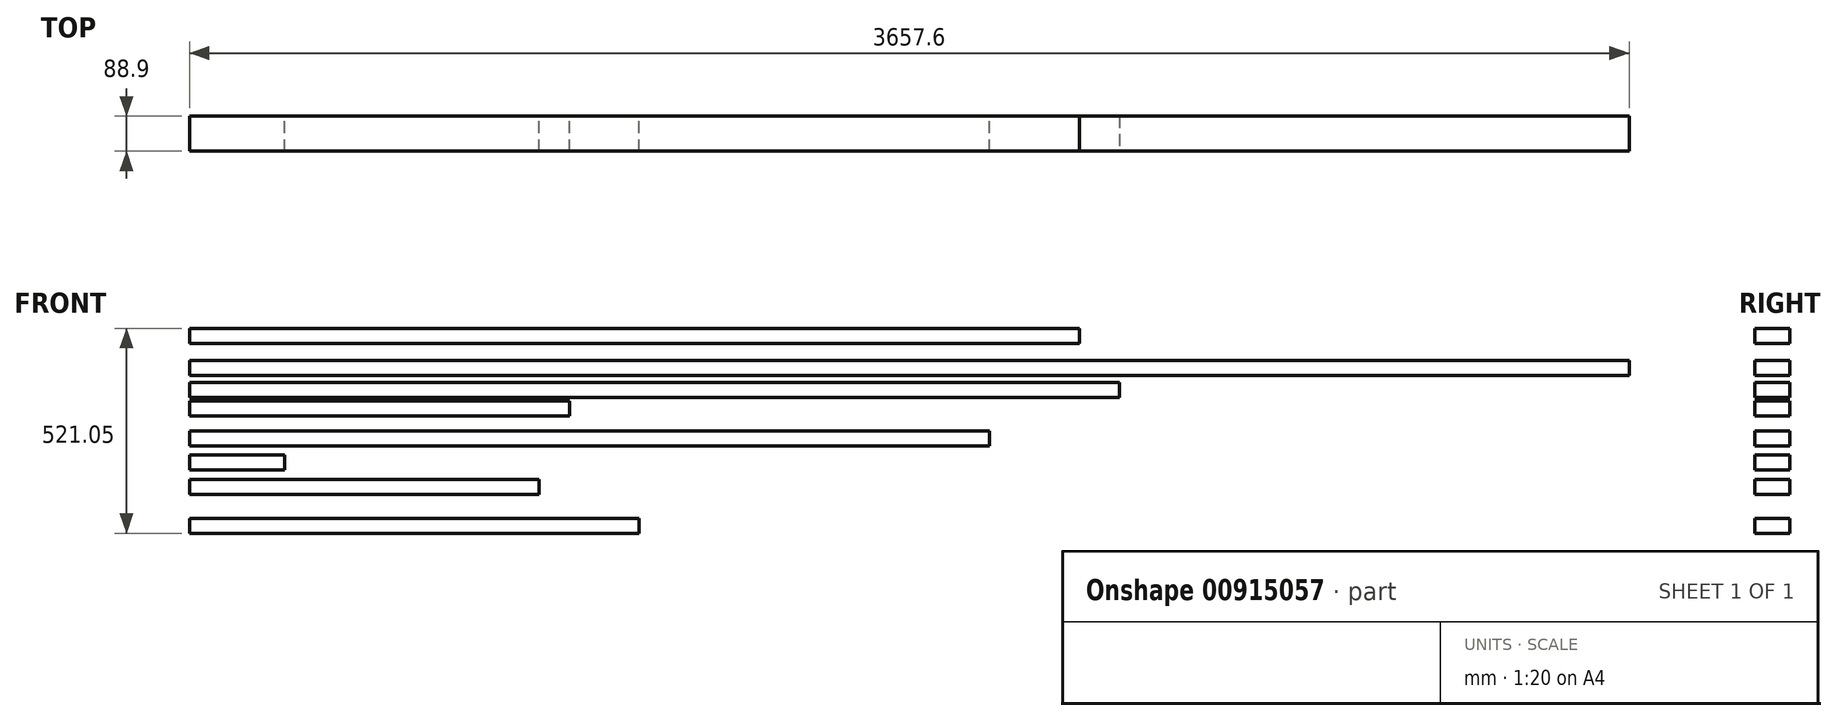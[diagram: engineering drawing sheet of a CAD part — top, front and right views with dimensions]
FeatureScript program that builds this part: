
annotation { "Feature Type Name" : "Feature", "Feature Type Description" : "" }
export const myFeature = defineFeature(function(context is Context, id is Id, definition is map)
    precondition{}
    {
        {
            var Q0;
            Q0=qCreatedBy(makeId("Right.planeOp"),FACE);
            var sketch = newSketch(context, id + "F0", { "sketchPlane" : qUnion([Q0])});
            skLineSegment(sketch, "E0.bottom", {"start": v(-44.45, -19.05) * mm, "end": v(44.45, -19.05) * mm});
            skLineSegment(sketch, "E0.top", {"start": v(-44.45, 19.05) * mm, "end": v(44.45, 19.05) * mm});
            skLineSegment(sketch, "E0.left", {"start": v(-44.45, -19.05) * mm, "end": v(-44.45, 19.05) * mm});
            skLineSegment(sketch, "E0.right", {"start": v(44.45, -19.05) * mm, "end": v(44.45, 19.05) * mm});
            skPoint(sketch, "E0.middle", {"position": v(0, 0) * mm});
            skSolve(sketch);
        }
        {
            var Q0;
            Q0=makeQuery(id+"F0.imprint","IMPRINT",FACE,{"disambiguationData":[TD([[makeQuery(id+"F0.imprint","IMPRINT",EDGE,{"derivedFrom":sQuery(id+"F0.wireOp",EDGE,"E0.bottom")}),1.0]])]});
            extrude(context, id + "F1", {"entities" : qUnion([Q0]), "depth" : 3657.6 * mm, "offsetDistance" : 25.4 * mm});
        }
        {
            var Q0;
            Q0=makeQuery(id+"F1.opExtrude","SWEPT_BODY",BODY,{"disambiguationData":[OSD([sQuery(id+"F0.wireOp",EDGE,"E0.bottom"),sQuery(id+"F0.wireOp",EDGE,"E0.top"),sQuery(id+"F0.wireOp",EDGE,"E0.left"),sQuery(id+"F0.wireOp",EDGE,"E0.right")])]});
            transform(context, id + "F2", {"entities" : qUnion([Q0]), "transformType" : TransformType.TRANSLATION_3D, "dx" : 0 * mm, "dy" : 0 * mm, "dz" : 52.83 * mm, "makeCopy" : true});
        }
        {
            var Q0;
            Q0=makeQuery(id+"F2.opPattern","COPY",BODY,{"derivedFrom":makeQuery(id+"F1.opExtrude","SWEPT_BODY",BODY,{"disambiguationData":[OSD([sQuery(id+"F0.wireOp",EDGE,"E0.bottom"),sQuery(id+"F0.wireOp",EDGE,"E0.top"),sQuery(id+"F0.wireOp",EDGE,"E0.left"),sQuery(id+"F0.wireOp",EDGE,"E0.right")])]}),"instanceName":"1"});
            deleteBodies(context, id + "F3", {"entities" : qUnion([Q0])});
        }
        {
            var Q0;
            Q0=qCreatedBy(makeId("Right.planeOp"),FACE);
            var sketch = newSketch(context, id + "F4", { "sketchPlane" : qUnion([Q0])});
            skLineSegment(sketch, "E1.bottom", {"start": v(44.45, -75.15) * mm, "end": v(-44.45, -75.15) * mm});
            skLineSegment(sketch, "E1.top", {"start": v(44.45, -37.05) * mm, "end": v(-44.45, -37.05) * mm});
            skLineSegment(sketch, "E1.left", {"start": v(44.45, -75.15) * mm, "end": v(44.45, -37.05) * mm});
            skLineSegment(sketch, "E1.right", {"start": v(-44.45, -75.15) * mm, "end": v(-44.45, -37.05) * mm});
            skPoint(sketch, "E1.middle", {"position": v(0, -56.1) * mm});
            skSolve(sketch);
        }
        {
            var Q0;
            Q0=makeQuery(id+"F4.imprint","IMPRINT",FACE,{"disambiguationData":[TD([[makeQuery(id+"F4.imprint","IMPRINT",EDGE,{"derivedFrom":sQuery(id+"F4.wireOp",EDGE,"E1.bottom")}),-1.0]])]});
            extrude(context, id + "F5", {"entities" : qUnion([Q0]), "depth" : 2362.2 * mm, "offsetDistance" : 25.4 * mm});
        }
        {
            var Q0;
            Q0=qCreatedBy(makeId("Right.planeOp"),FACE);
            var sketch = newSketch(context, id + "F6", { "sketchPlane" : qUnion([Q0])});
            skLineSegment(sketch, "E2.bottom", {"start": v(44.45, 63.17) * mm, "end": v(-44.45, 63.17) * mm});
            skLineSegment(sketch, "E2.top", {"start": v(44.45, 101.27) * mm, "end": v(-44.45, 101.27) * mm});
            skLineSegment(sketch, "E2.left", {"start": v(44.45, 63.17) * mm, "end": v(44.45, 101.27) * mm});
            skLineSegment(sketch, "E2.right", {"start": v(-44.45, 63.17) * mm, "end": v(-44.45, 101.27) * mm});
            skPoint(sketch, "E2.middle", {"position": v(0, 82.22) * mm});
            skSolve(sketch);
        }
        {
            var Q0;
            Q0=makeQuery(id+"F6.imprint","IMPRINT",FACE,{"disambiguationData":[TD([[makeQuery(id+"F6.imprint","IMPRINT",EDGE,{"derivedFrom":sQuery(id+"F6.wireOp",EDGE,"E2.bottom")}),-1.0]])]});
            extrude(context, id + "F7", {"entities" : qUnion([Q0]), "depth" : 2260.6 * mm, "offsetDistance" : 25.4 * mm});
        }
        {
            var Q0;
            Q0=qCreatedBy(makeId("Right.planeOp"),FACE);
            var sketch = newSketch(context, id + "F8", { "sketchPlane" : qUnion([Q0])});
            skLineSegment(sketch, "E3.bottom", {"start": v(-44.45, -121.04) * mm, "end": v(44.45, -121.04) * mm});
            skLineSegment(sketch, "E3.top", {"start": v(-44.45, -82.94) * mm, "end": v(44.45, -82.94) * mm});
            skLineSegment(sketch, "E3.left", {"start": v(-44.45, -121.04) * mm, "end": v(-44.45, -82.94) * mm});
            skLineSegment(sketch, "E3.right", {"start": v(44.45, -121.04) * mm, "end": v(44.45, -82.94) * mm});
            skPoint(sketch, "E3.middle", {"position": v(0, -102) * mm});
            skSolve(sketch);
        }
        {
            var Q0;
            Q0=makeQuery(id+"F8.imprint","IMPRINT",FACE,{"disambiguationData":[TD([[makeQuery(id+"F8.imprint","IMPRINT",EDGE,{"derivedFrom":sQuery(id+"F8.wireOp",EDGE,"E3.bottom")}),1.0]])]});
            extrude(context, id + "F9", {"entities" : qUnion([Q0]), "depth" : 965.2 * mm, "offsetDistance" : 25.4 * mm});
        }
        {
            var Q0;
            Q0=qCreatedBy(makeId("Right.planeOp"),FACE);
            var sketch = newSketch(context, id + "F10", { "sketchPlane" : qUnion([Q0])});
            skLineSegment(sketch, "E4.bottom", {"start": v(-44.45, -197.84) * mm, "end": v(44.45, -197.84) * mm});
            skLineSegment(sketch, "E4.top", {"start": v(-44.45, -159.74) * mm, "end": v(44.45, -159.74) * mm});
            skLineSegment(sketch, "E4.left", {"start": v(-44.45, -197.84) * mm, "end": v(-44.45, -159.74) * mm});
            skLineSegment(sketch, "E4.right", {"start": v(44.45, -197.84) * mm, "end": v(44.45, -159.74) * mm});
            skPoint(sketch, "E4.middle", {"position": v(0, -178.79) * mm});
            skSolve(sketch);
        }
        {
            var Q0;
            Q0=makeQuery(id+"F10.imprint","IMPRINT",FACE,{"disambiguationData":[TD([[makeQuery(id+"F10.imprint","IMPRINT",EDGE,{"derivedFrom":sQuery(id+"F10.wireOp",EDGE,"E4.bottom")}),1.0]])]});
            extrude(context, id + "F11", {"entities" : qUnion([Q0]), "depth" : 2032 * mm, "offsetDistance" : 25.4 * mm});
        }
        {
            var Q0;
            Q0=qCreatedBy(makeId("Right.planeOp"),FACE);
            var sketch = newSketch(context, id + "F12", { "sketchPlane" : qUnion([Q0])});
            skLineSegment(sketch, "E5.bottom", {"start": v(-44.45, -258.06) * mm, "end": v(44.45, -258.06) * mm});
            skLineSegment(sketch, "E5.top", {"start": v(-44.45, -219.96) * mm, "end": v(44.45, -219.96) * mm});
            skLineSegment(sketch, "E5.left", {"start": v(-44.45, -258.06) * mm, "end": v(-44.45, -219.96) * mm});
            skLineSegment(sketch, "E5.right", {"start": v(44.45, -258.06) * mm, "end": v(44.45, -219.96) * mm});
            skPoint(sketch, "E5.middle", {"position": v(0, -239) * mm});
            skSolve(sketch);
        }
        {
            var Q0;
            Q0=makeQuery(id+"F12.imprint","IMPRINT",FACE,{"disambiguationData":[TD([[makeQuery(id+"F12.imprint","IMPRINT",EDGE,{"derivedFrom":sQuery(id+"F12.wireOp",EDGE,"E5.bottom")}),1.0]])]});
            extrude(context, id + "F13", {"entities" : qUnion([Q0]), "depth" : 241.3 * mm, "offsetDistance" : 25.4 * mm});
        }
        {
            var Q0;
            Q0=qCreatedBy(makeId("Right.planeOp"),FACE);
            var sketch = newSketch(context, id + "F14", { "sketchPlane" : qUnion([Q0])});
            skLineSegment(sketch, "E6.bottom", {"start": v(-44.45, -320.49) * mm, "end": v(44.45, -320.49) * mm});
            skLineSegment(sketch, "E6.top", {"start": v(-44.45, -282.39) * mm, "end": v(44.45, -282.39) * mm});
            skLineSegment(sketch, "E6.left", {"start": v(-44.45, -320.49) * mm, "end": v(-44.45, -282.39) * mm});
            skLineSegment(sketch, "E6.right", {"start": v(44.45, -320.49) * mm, "end": v(44.45, -282.39) * mm});
            skPoint(sketch, "E6.middle", {"position": v(0, -301.44) * mm});
            skSolve(sketch);
        }
        {
            var Q0;
            Q0=makeQuery(id+"F14.imprint","IMPRINT",FACE,{"disambiguationData":[TD([[makeQuery(id+"F14.imprint","IMPRINT",EDGE,{"derivedFrom":sQuery(id+"F14.wireOp",EDGE,"E6.bottom")}),1.0]])]});
            extrude(context, id + "F15", {"entities" : qUnion([Q0]), "depth" : 889 * mm, "offsetDistance" : 25.4 * mm});
        }
        {
            var Q0;
            Q0=qCreatedBy(makeId("Right.planeOp"),FACE);
            var sketch = newSketch(context, id + "F16", { "sketchPlane" : qUnion([Q0])});
            skLineSegment(sketch, "E7.bottom", {"start": v(-44.45, -419.78) * mm, "end": v(44.45, -419.78) * mm});
            skLineSegment(sketch, "E7.top", {"start": v(-44.45, -381.68) * mm, "end": v(44.45, -381.68) * mm});
            skLineSegment(sketch, "E7.left", {"start": v(-44.45, -419.78) * mm, "end": v(-44.45, -381.68) * mm});
            skLineSegment(sketch, "E7.right", {"start": v(44.45, -419.78) * mm, "end": v(44.45, -381.68) * mm});
            skPoint(sketch, "E7.middle", {"position": v(0, -400.73) * mm});
            skSolve(sketch);
        }
        {
            var Q0;
            Q0=makeQuery(id+"F16.imprint","IMPRINT",FACE,{"disambiguationData":[TD([[makeQuery(id+"F16.imprint","IMPRINT",EDGE,{"derivedFrom":sQuery(id+"F16.wireOp",EDGE,"E7.bottom")}),1.0]])]});
            extrude(context, id + "F17", {"entities" : qUnion([Q0]), "depth" : 1143 * mm, "offsetDistance" : 25.4 * mm});
        }
    });
